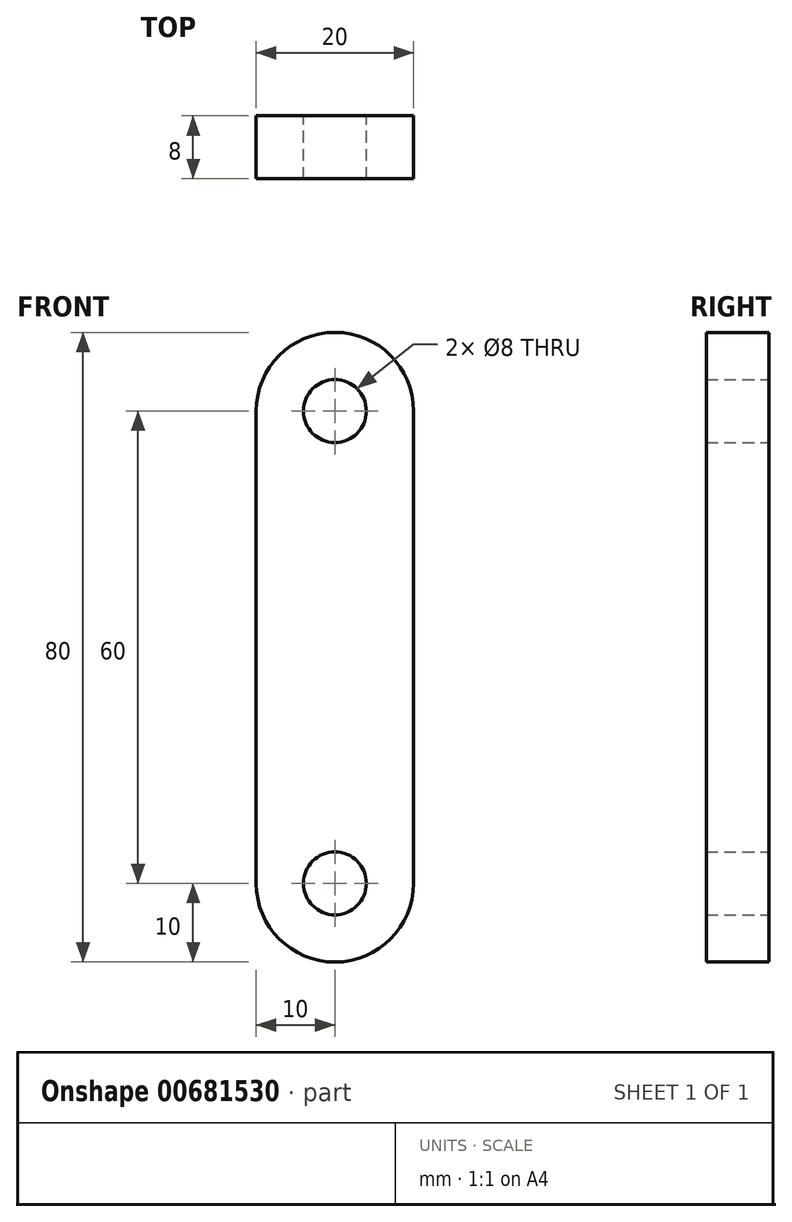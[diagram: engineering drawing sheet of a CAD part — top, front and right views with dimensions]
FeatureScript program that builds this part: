
annotation { "Feature Type Name" : "Feature", "Feature Type Description" : "" }
export const myFeature = defineFeature(function(context is Context, id is Id, definition is map)
    precondition{}
    {
        {
            var Q0;
            Q0=qCreatedBy(makeId("Front.planeOp"),FACE);
            var sketch = newSketch(context, id + "F0", { "sketchPlane" : qUnion([Q0])});
            skCircle(sketch, "E0", {"center": v(0, 0) * mm, "radius": 4 * mm});
            skCircle(sketch, "E1", {"center": v(0, 60) * mm, "radius": 4 * mm});
            skArc(sketch, "E2", {"start": v(10, 60) * mm, "mid": v(0, 70) * mm, "end": v(-10, 60) * mm});
            skArc(sketch, "E3", {"start": v(-10, 0) * mm, "mid": v(0, -10) * mm, "end": v(10, 0) * mm});
            skLineSegment(sketch, "E4", {"start": v(-10, 60) * mm, "end": v(-10, 0) * mm});
            skLineSegment(sketch, "E5", {"start": v(10, 60) * mm, "end": v(10, 0) * mm});
            skSolve(sketch);
        }
        {
            var Q0;
            Q0=makeQuery(id+"F0.imprint","IMPRINT",FACE,{"disambiguationData":[TD([[makeQuery(id+"F0.imprint","IMPRINT",EDGE,{"derivedFrom":sQuery(id+"F0.wireOp",EDGE,"E0")}),-1.0]])]});
            extrude(context, id + "F1", {"entities" : qUnion([Q0]), "endBound" : BoundingType.SYMMETRIC, "depth" : 8 * mm, "offsetDistance" : 25 * mm});
        }
    });
